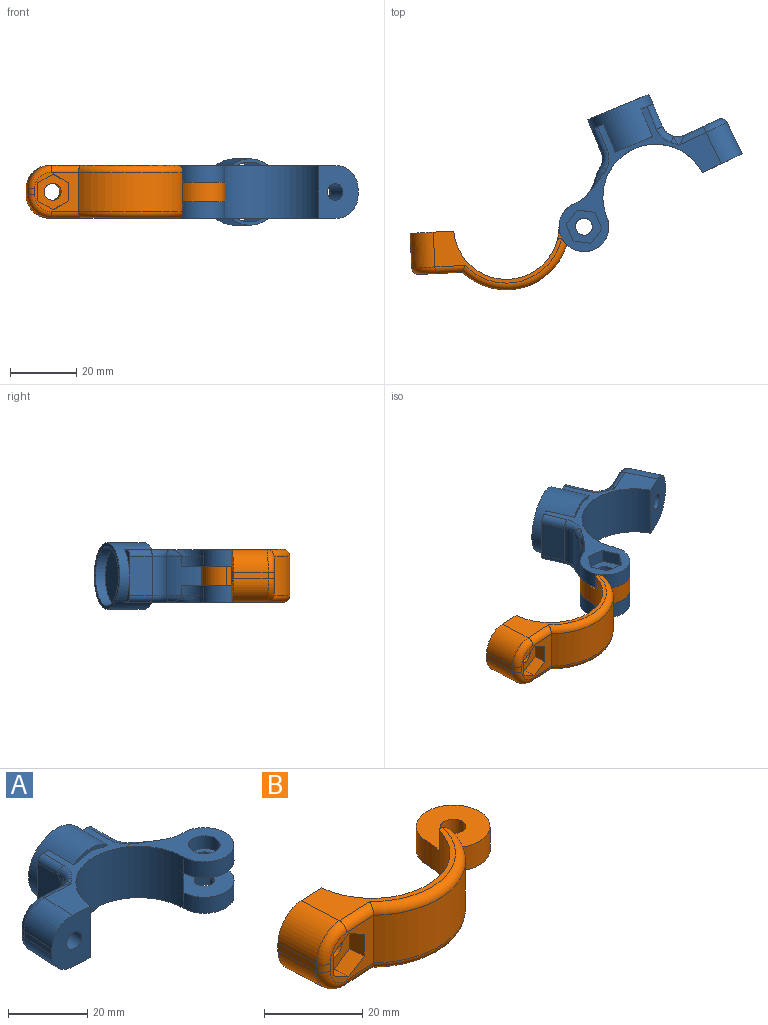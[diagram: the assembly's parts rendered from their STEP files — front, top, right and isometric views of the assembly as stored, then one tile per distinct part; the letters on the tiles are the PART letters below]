
ASSEMBLY  parts=2 mates=1
PART A: 69 faces, bbox 59.9x36.9x35.9 mm
  f0: bspline ~4.73x3mm, area 1.3mm2, adj f30,f32,f66,f67
  f1: cylinder r=5mm len=9.44mm, axis (0,0,-1), area 76.5mm2, adj f19,f20,f67,f68
  f2: plane 18.04x15.88mm, normal (0,1,0), area 243.1mm2, adj f6,f21,f60
  f3: plane 7.94x3.92mm, normal (0,1,0), area 8.5mm2, adj f6,f17,f42,f59
  f4: plane 7.94x3.92mm, normal (0,1,0), area 8.5mm2, adj f17,f21,f45,f59
  f5: plane 7.94x3.92mm, normal (0,1,0), area 8.5mm2, adj f6,f19,f34,f59
  f6: plane 52.89x33.66mm, normal (0,0,-1), area 372.7mm2, adj f2,f3,f5,f9,f12,f13,f27,f34
  f7: cylinder r=2.55mm len=5.11mm, axis (0,0,-1), area 15mm2, adj f24,f47
  f8: cylinder r=2.55mm len=8.73mm, axis (0.05,1,0), area 136.1mm2, adj f12,f26
  f9: cylinder r=7.5mm len=15mm, axis (0,0,-1), area 175.1mm2, adj f6,f13,f23,f57,f58
  f10: cylinder r=2.55mm len=5.11mm, axis (0,0,-1), area 15mm2, adj f23,f54
  f11: plane 10.47x1.88mm, normal (-1,0.05,0), area 19.7mm2, adj f12,f27,f28,f35
  f12: plane 15.88x13.18mm, normal (-0.05,-1,0), area 168mm2, adj f6,f8,f11,f13,f21,f27,f28
  f13: cylinder r=15.88mm len=31.69mm, axis (0,0,-1), area 770.4mm2, adj f6,f9,f12,f14,f21,f22
  f14: cylinder r=7.5mm len=15mm, axis (0,0,-1), area 175.1mm2, adj f13,f21,f24,f55,f56
  f15: cylinder r=19mm len=11.88mm, axis (0,0,-1), area 96.7mm2, adj f16,f22,f23,f24,f40,f43,f55,f57
  f16: cylinder r=5mm len=11.88mm, axis (0,0,-1), area 53.2mm2, adj f15,f17,f41,f44
  f17: plane 11.88x7.42mm, normal (1,0,0), area 88.1mm2, adj f3,f4,f16,f42,f45
  f18: plane 7.94x3.92mm, normal (0,1,0), area 8.5mm2, adj f19,f21,f29,f59
  f19: plane 11.88x7.35mm, normal (-1,0,0), area 87.3mm2, adj f1,f5,f18,f29,f34,f67,f68
  f20: plane 11.88x11.13mm, normal (0.05,1,0), area 71.3mm2, adj f1,f25,f32,f33,f35,f37,f39,f67
  f21: plane 52.89x33.66mm, normal (0,0,1), area 398.6mm2, adj f2,f4,f12,f13,f14,f18,f28,f29
  f22: cylinder r=7.5mm len=6mm, axis (0,0,1), area 36.5mm2, adj f13,f15,f23,f24
  f23: plane 18.96x15.72mm, normal (0,0,1), area 164.8mm2, adj f9,f10,f15,f22,f57
  f24: plane 18.96x15.72mm, normal (0,0,-1), area 164.8mm2, adj f7,f14,f15,f22,f55
  f25: cylinder r=4mm len=8.19mm, axis (0.05,1,0), area 100.5mm2, adj f20,f26
  f26: plane 8x7.99mm, normal (0.05,1,0), area 29.8mm2, adj f8,f25
  f27: cylinder r=7mm len=10.82mm, axis (-0.05,-1,0), area 115.3mm2, adj f6,f11,f12,f37
  f28: cylinder r=7mm len=10.82mm, axis (0.05,1,0), area 115.3mm2, adj f11,f12,f21,f33
  f29: cylinder r=2mm len=7.42mm, axis (0,1,0), area 23.3mm2, adj f18,f19,f21,f30,f67
  f30: torus R=7mm, axis (0,0,1), area 14.3mm2, adj f0,f21,f29,f31,f67
  f31: torus R=17mm, axis (0,0,1), area 3.2mm2, adj f21,f30,f66
  f32: cylinder r=2mm len=9.22mm, axis (1,-0.05,0), area 22.7mm2, adj f0,f20,f21,f33,f66,f67
  f33: torus R=5mm, axis (0.05,1,0), area 31mm2, adj f20,f28,f32,f35
  f34: cylinder r=2mm len=7.42mm, axis (0,-1,0), area 23.3mm2, adj f5,f6,f19,f36,f68
  f35: cylinder r=2mm len=2.1mm, axis (0,0,-1), area 5.9mm2, adj f11,f20,f33,f37
  f36: torus R=7mm, axis (0,0,1), area 14.3mm2, adj f6,f34,f38,f65,f68
  f37: torus R=5mm, axis (0.05,1,0), area 31mm2, adj f20,f27,f35,f39
  f38: torus R=17mm, axis (0,0,1), area 3.2mm2, adj f6,f36,f64
  f39: cylinder r=2mm len=9.22mm, axis (-1,0.05,0), area 22.7mm2, adj f6,f20,f37,f64,f65,f68
  f40: torus R=17mm, axis (0,0,1), area 9.4mm2, adj f6,f15,f41,f58
  f41: torus R=7mm, axis (0,0,1), area 16.1mm2, adj f6,f16,f40,f42
  f42: cylinder r=2mm len=7.42mm, axis (0,1,0), area 23.3mm2, adj f3,f6,f17,f41
  f43: torus R=17mm, axis (0,0,1), area 9.4mm2, adj f15,f21,f44,f56
  f44: torus R=7mm, axis (0,0,1), area 16.1mm2, adj f16,f21,f43,f45
  f45: cylinder r=2mm len=7.42mm, axis (0,-1,0), area 23.3mm2, adj f4,f17,f21,f44
  f46: cylinder r=4mm len=8mm, axis (0,0,1), area 100.5mm2, adj f21,f47
  f47: plane 8x8mm, normal (0,0,1), area 29.8mm2, adj f7,f46
  f48: plane 5.43x4mm, normal (1,0,0), area 21.7mm2, adj f6,f49,f53,f54
  f49: plane 4.7x4mm, normal (0.5,0.87,0), area 21.7mm2, adj f6,f48,f50,f54
  f50: plane 4.7x4mm, normal (-0.5,0.87,0), area 21.7mm2, adj f6,f49,f51,f54
  f51: plane 5.43x4mm, normal (-1,0,0), area 21.7mm2, adj f6,f50,f52,f54
  f52: plane 4.7x4mm, normal (-0.5,-0.87,0), area 21.7mm2, adj f6,f51,f53,f54
  f53: plane 4.7x4mm, normal (0.5,-0.87,0), area 21.7mm2, adj f6,f48,f52,f54
  f54: plane 10.85x9.4mm, normal (0,0,-1), area 56.1mm2, adj f10,f48,f49,f50,f51,f52,f53
  f55: cylinder r=10mm len=8.12mm, axis (0,0,1), area 27.5mm2, adj f14,f15,f24,f56
  f56: bspline ~12x11.95mm, area 22.2mm2, adj f14,f21,f43,f55
  f57: cylinder r=10mm len=8.12mm, axis (0,0,1), area 27.5mm2, adj f9,f15,f23,f58
  f58: bspline ~12x11.95mm, area 22.2mm2, adj f6,f9,f40,f57
  f59: cylinder r=10mm len=20mm, axis (0,1,0), area 436.4mm2, adj f3,f4,f5,f6,f18,f21,f61,f62
  f60: cylinder r=9.02mm len=18.04mm, axis (0,1,0), area 342.1mm2, adj f2,f6,f21,f61,f62,f63
  f61: plane 12.17x2.06mm, normal (0,-1,0), area 10.8mm2, adj f21,f59,f60
  f62: plane 12.17x2.06mm, normal (0,-1,0), area 10.8mm2, adj f6,f59,f60
  f63: plane 20x20mm, normal (0,1,0), area 58.6mm2, adj f59,f60
  f64: bspline ~3.35x3.21mm, area 3.7mm2, adj f38,f39,f65
  f65: bspline ~4.72x2.96mm, area 1.3mm2, adj f36,f39,f64,f68
  f66: bspline ~3.35x3.21mm, area 3.7mm2, adj f0,f31,f32
  f67: bspline ~5.44x5.2mm, area 12.2mm2, adj f0,f1,f19,f20,f29,f30,f32
  f68: bspline ~5.44x5.2mm, area 12.2mm2, adj f1,f19,f20,f34,f36,f39,f65
PART B: 32 faces, bbox 59.9x28.1x17 mm
  f0: plane 13.23x11.88mm, normal (0.05,-1,0), area 70mm2, adj f3,f14,f15,f16,f17,f18,f19,f24
  f1: cylinder r=2.55mm len=8.73mm, axis (0.05,-1,0), area 136.1mm2, adj f6,f20
  f2: cylinder r=7.5mm len=4.91mm, axis (0,0,1), area 7.9mm2, adj f3,f12,f28,f31
  f3: cylinder r=19mm len=31.36mm, axis (0,0,1), area 461.5mm2, adj f0,f2,f4,f11,f23,f28
  f4: cylinder r=7.5mm len=4.91mm, axis (0,0,1), area 7.9mm2, adj f3,f13,f23,f30
  f5: cylinder r=15.88mm len=31.69mm, axis (0,0,1), area 726.6mm2, adj f6,f8,f9,f11,f12,f13,f30,f31
  f6: plane 15.88x13.18mm, normal (-0.05,1,0), area 168mm2, adj f1,f5,f7,f8,f9,f21,f22
  f7: plane 10.47x1.88mm, normal (-1,-0.05,0), area 19.7mm2, adj f6,f21,f22,f26
  f8: plane 38.61x15.66mm, normal (0,0,-1), area 119.6mm2, adj f5,f6,f22,f28,f29,f31
  f9: plane 38.61x15.66mm, normal (0,0,1), area 119.6mm2, adj f5,f6,f21,f23,f24,f30
  f10: cylinder r=2.55mm len=5.9mm, axis (0,0,1), area 94.6mm2, adj f12,f13
  f11: cylinder r=7.5mm len=15mm, axis (0,0,1), area 242.2mm2, adj f3,f5,f12,f13
  f12: plane 15.6x15mm, normal (0,0,-1), area 158mm2, adj f2,f5,f10,f11,f31
  f13: plane 15.6x15mm, normal (0,0,1), area 158mm2, adj f4,f5,f10,f11,f30
  f14: plane 4.89x4.23mm, normal (0.5,0.02,0.87), area 21.7mm2, adj f0,f15,f19,f20
  f15: plane 4.89x4.23mm, normal (-0.5,-0.02,0.87), area 21.7mm2, adj f0,f14,f16,f20
  f16: plane 5.43x4mm, normal (-1,-0.05,0), area 21.7mm2, adj f0,f15,f17,f20
  f17: plane 4.89x4.23mm, normal (-0.5,-0.02,-0.87), area 21.7mm2, adj f0,f16,f18,f20
  f18: plane 4.89x4.23mm, normal (0.5,0.02,-0.87), area 21.7mm2, adj f0,f17,f19,f20
  f19: plane 5.43x4mm, normal (1,0.05,0), area 21.7mm2, adj f0,f14,f18,f20
  f20: plane 10.85x9.39mm, normal (0.05,-1,0), area 56.1mm2, adj f1,f14,f15,f16,f17,f18,f19
  f21: cylinder r=7mm len=10.82mm, axis (0.05,-1,0), area 115.3mm2, adj f6,f7,f9,f25
  f22: cylinder r=7mm len=10.82mm, axis (-0.05,1,0), area 115.3mm2, adj f6,f7,f8,f27
  f23: torus R=17mm, axis (0,0,1), area 119.8mm2, adj f3,f4,f9,f24,f30
  f24: cylinder r=2mm len=9.22mm, axis (1,0.05,0), area 26.9mm2, adj f0,f9,f23,f25
  f25: torus R=5mm, axis (0.05,-1,0), area 31mm2, adj f0,f21,f24,f26
  f26: cylinder r=2mm len=2.1mm, axis (0,0,1), area 5.9mm2, adj f0,f7,f25,f27
  f27: torus R=5mm, axis (0.05,-1,0), area 31mm2, adj f0,f22,f26,f29
  f28: torus R=17mm, axis (0,0,1), area 119.8mm2, adj f2,f3,f8,f29,f31
  f29: cylinder r=2mm len=9.22mm, axis (-1,-0.05,0), area 26.9mm2, adj f0,f8,f27,f28
  f30: cylinder r=1mm len=4.99mm, axis (0,0,1), area 11.4mm2, adj f4,f5,f9,f13,f23
  f31: cylinder r=1mm len=4.99mm, axis (0,0,1), area 11.4mm2, adj f2,f5,f8,f12,f28
PLACE A rot(axis=(0.2,-0.98,0),180deg) t=(24.07,-1.91,23.08)mm
PLACE B t=(-20.9,-10.86,23.13)mm
MATE revolute B.f10 <-> A.f22  axis (0,0,1) through (2.48,-10.86,18.15)mm
